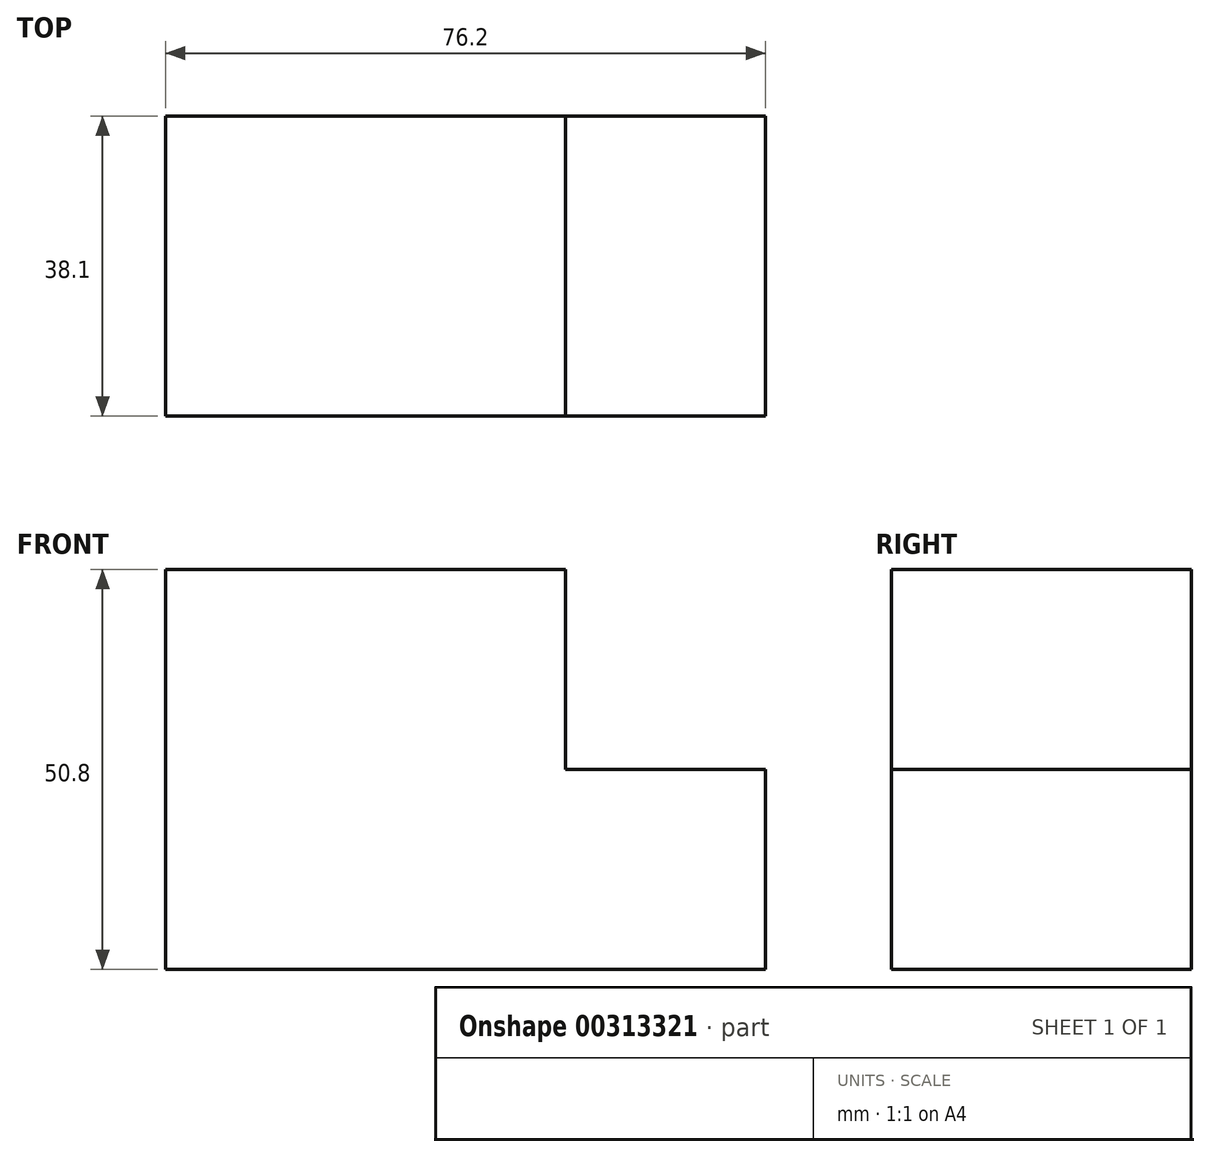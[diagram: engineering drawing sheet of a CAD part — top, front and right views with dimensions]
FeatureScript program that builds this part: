
annotation { "Feature Type Name" : "Feature", "Feature Type Description" : "" }
export const myFeature = defineFeature(function(context is Context, id is Id, definition is map)
    precondition{}
    {
        {
            var Q0;
            Q0=qCreatedBy(makeId("Front.planeOp"),FACE);
            var sketch = newSketch(context, id + "F0", { "sketchPlane" : qUnion([Q0])});
            skLineSegment(sketch, "E0", {"start": v(-41.27, -42.67) * mm, "end": v(34.93, -42.67) * mm});
            skLineSegment(sketch, "E1", {"start": v(34.93, -42.67) * mm, "end": v(34.93, -17.27) * mm});
            skLineSegment(sketch, "E2", {"start": v(34.93, -17.27) * mm, "end": v(9.53, -17.27) * mm});
            skLineSegment(sketch, "E3", {"start": v(9.53, -17.27) * mm, "end": v(9.53, 8.13) * mm});
            skLineSegment(sketch, "E4", {"start": v(9.53, 8.13) * mm, "end": v(-41.27, 8.13) * mm});
            skLineSegment(sketch, "E5", {"start": v(-41.27, 8.13) * mm, "end": v(-41.27, -42.67) * mm});
            skSolve(sketch);
        }
        {
            var Q0;
            Q0=makeQuery(id+"F0.imprint","IMPRINT",FACE,{"disambiguationData":[TD([[makeQuery(id+"F0.imprint","IMPRINT",EDGE,{"derivedFrom":sQuery(id+"F0.wireOp",EDGE,"E0")}),1.0]])]});
            extrude(context, id + "F1", {"entities" : qUnion([Q0]), "depth" : 38.1 * mm});
        }
    });
